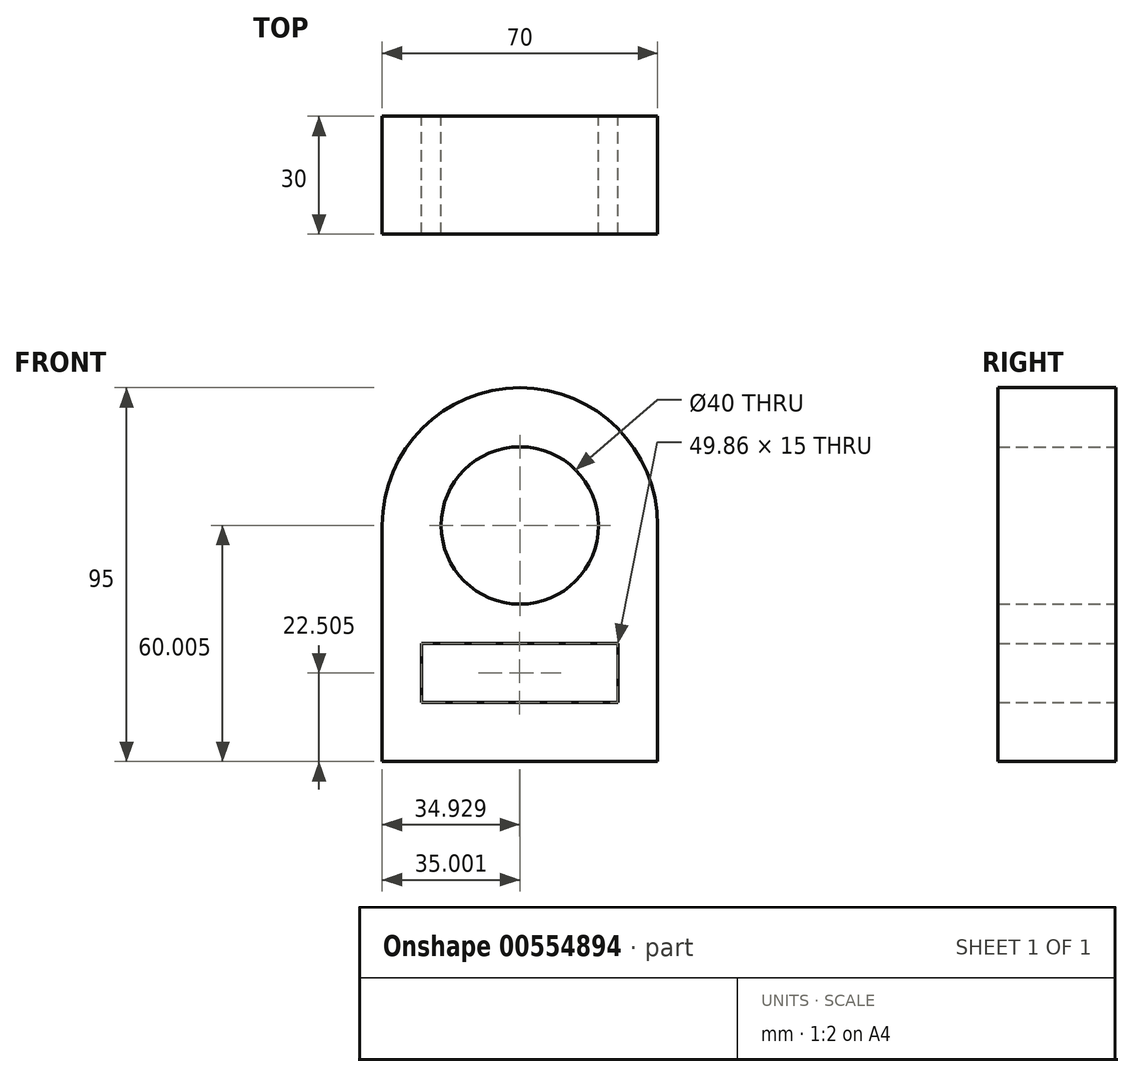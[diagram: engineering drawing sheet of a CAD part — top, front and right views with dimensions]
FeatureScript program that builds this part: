
annotation { "Feature Type Name" : "Feature", "Feature Type Description" : "" }
export const myFeature = defineFeature(function(context is Context, id is Id, definition is map)
    precondition{}
    {
        {
            var Q0;
            Q0=qCreatedBy(makeId("Front.planeOp"),FACE);
            var sketch = newSketch(context, id + "F0", { "sketchPlane" : qUnion([Q0])});
            skLineSegment(sketch, "E0", {"start": v(-62.69, -20.94) * mm, "end": v(-62.69, 39.06) * mm});
            skLineSegment(sketch, "E1", {"start": v(-62.69, -20.94) * mm, "end": v(7.31, -20.94) * mm});
            skLineSegment(sketch, "E2", {"start": v(7.31, -20.94) * mm, "end": v(7.31, 39.06) * mm});
            skLineSegment(sketch, "E3", {"start": v(-52.69, 9.06) * mm, "end": v(-52.69, -5.94) * mm});
            skLineSegment(sketch, "E4", {"start": v(-52.69, -5.94) * mm, "end": v(-2.83, -5.94) * mm});
            skLineSegment(sketch, "E5", {"start": v(-2.83, -5.94) * mm, "end": v(-2.83, 9.06) * mm});
            skLineSegment(sketch, "E6", {"start": v(-2.83, 9.06) * mm, "end": v(-52.69, 9.06) * mm});
            skPoint(sketch, "E7", {"position": v(-27.69, 39.06) * mm});
            skCircle(sketch, "E8", {"center": v(-27.69, 39.06) * mm, "radius": 20 * mm});
            skArc(sketch, "E9", {"start": v(7.31, 39.06) * mm, "mid": v(-27.69, 74.06) * mm, "end": v(-62.69, 39.06) * mm});
            skSolve(sketch);
        }
        {
            var Q0;
            Q0 = qSketchRegion(id + "F0", true);
            extrude(context, id + "F1", {"entities" : qUnion([Q0]), "depth" : 30 * mm, "offsetDistance" : 25 * mm});
        }
    });
